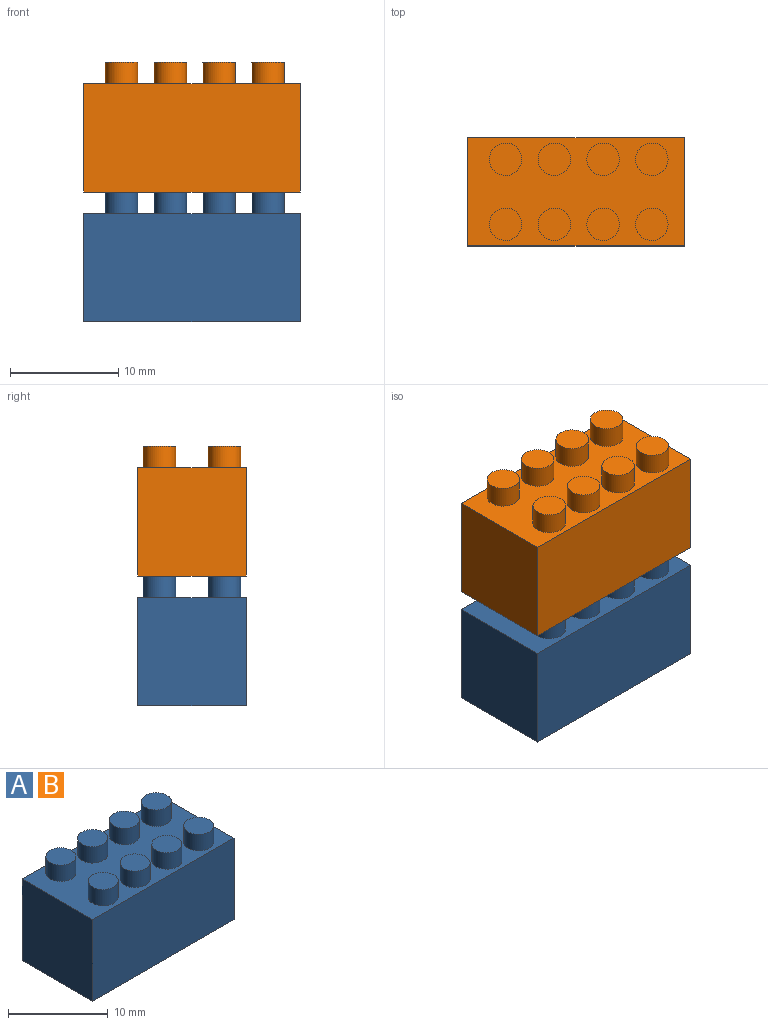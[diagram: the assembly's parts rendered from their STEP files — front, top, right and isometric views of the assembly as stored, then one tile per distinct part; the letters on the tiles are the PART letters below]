
ASSEMBLY  parts=2 mates=1
PART A: 38 faces, bbox 20x10x12 mm
  f0: plane 10x10mm, normal (-1,0,0), area 100mm2, adj f1,f3,f4,f5
  f1: plane 20x10mm, normal (0,-1,0), area 200mm2, adj f0,f2,f4,f5
  f2: plane 10x10mm, normal (1,0,0), area 100mm2, adj f1,f3,f4,f5
  f3: plane 20x10mm, normal (0,1,0), area 200mm2, adj f0,f2,f4,f5
  f4: plane 20x10mm, normal (0,0,1), area 143.5mm2, adj f0,f1,f2,f3,f6,f8,f10,f12
  f5: plane 20x10mm, normal (0,0,-1), area 143.5mm2, adj f0,f1,f2,f3,f22,f24,f26,f28
  f6: cylinder r=1.5mm len=3mm, axis (0,0,-1), area 18.8mm2, adj f4,f7
  f7: plane 3x3mm, normal (0,0,1), area 7.1mm2, adj f6
  f8: cylinder r=1.5mm len=3mm, axis (0,0,-1), area 18.8mm2, adj f4,f9
  f9: plane 3x3mm, normal (0,0,1), area 7.1mm2, adj f8
  f10: cylinder r=1.5mm len=3mm, axis (0,0,-1), area 18.8mm2, adj f4,f11
  f11: plane 3x3mm, normal (0,0,1), area 7.1mm2, adj f10
  f12: cylinder r=1.5mm len=3mm, axis (0,0,-1), area 18.8mm2, adj f4,f13
  f13: plane 3x3mm, normal (0,0,1), area 7.1mm2, adj f12
  f14: cylinder r=1.5mm len=3mm, axis (0,0,-1), area 18.8mm2, adj f4,f15
  f15: plane 3x3mm, normal (0,0,1), area 7.1mm2, adj f14
  f16: cylinder r=1.5mm len=3mm, axis (0,0,-1), area 18.8mm2, adj f4,f17
  f17: plane 3x3mm, normal (0,0,1), area 7.1mm2, adj f16
  f18: cylinder r=1.5mm len=3mm, axis (0,0,-1), area 18.8mm2, adj f4,f19
  f19: plane 3x3mm, normal (0,0,1), area 7.1mm2, adj f18
  f20: cylinder r=1.5mm len=3mm, axis (0,0,-1), area 18.8mm2, adj f4,f21
  f21: plane 3x3mm, normal (0,0,1), area 7.1mm2, adj f20
  f22: cylinder r=1.5mm len=3mm, axis (0,0,-1), area 28.3mm2, adj f5,f23
  f23: plane 3x3mm, normal (0,0,-1), area 7.1mm2, adj f22
  f24: cylinder r=1.5mm len=3mm, axis (0,0,-1), area 28.3mm2, adj f5,f25
  f25: plane 3x3mm, normal (0,0,-1), area 7.1mm2, adj f24
  f26: cylinder r=1.5mm len=3mm, axis (0,0,-1), area 28.3mm2, adj f5,f27
  f27: plane 3x3mm, normal (0,0,-1), area 7.1mm2, adj f26
  f28: cylinder r=1.5mm len=3mm, axis (0,0,-1), area 28.3mm2, adj f5,f29
  f29: plane 3x3mm, normal (0,0,-1), area 7.1mm2, adj f28
  f30: cylinder r=1.5mm len=3mm, axis (0,0,-1), area 28.3mm2, adj f5,f31
  f31: plane 3x3mm, normal (0,0,-1), area 7.1mm2, adj f30
  f32: cylinder r=1.5mm len=3mm, axis (0,0,-1), area 28.3mm2, adj f5,f33
  f33: plane 3x3mm, normal (0,0,-1), area 7.1mm2, adj f32
  f34: cylinder r=1.5mm len=3mm, axis (0,0,-1), area 28.3mm2, adj f5,f35
  f35: plane 3x3mm, normal (0,0,-1), area 7.1mm2, adj f34
  f36: cylinder r=1.5mm len=3mm, axis (0,0,-1), area 28.3mm2, adj f5,f37
  f37: plane 3x3mm, normal (0,0,-1), area 7.1mm2, adj f36
PART B: same geometry as A
PLACE A t=(-10.29,-9.65,-1.37)mm fixed
PLACE B t=(-10.29,-9.65,10.63)mm
MATE revolute B.f14 <-> A.f14  axis (0,0,-1) through (-6.79,-7.65,10.63)mm
